# Revit family: 712-1520-001-DN80-250
name_source: partatom
category: Pipe Accessories
units: mm (PartAtom-declared; Revit-internal decimal feet)

## family parameters
Always vertical = Yes
Cut with Voids When Loaded = No
Part Type = Valve - Breaks Into
Round Connector Dimension = Use Diameter
Shared = No
Work Plane-Based = No

## types (8) — shared parameters
Body_wallthickness = 10 mm  [stored 0.0328084 ft]
DN080_PN10/16 = 712-0080-15-201
DN100_PN10/16 = 712-0100-15-201
DN125_PN10/16 = 712-0125-15-201
DN150_PN10/16 = 712-0150-15-201
DN200_PN10 = 712-0200-15-200
DN200_PN16 = 712-0200-15-201
DN250_PN10 = 712-0250-15-200
Description_ = AVK CROSS Loose flange
RF_Thick = 3 mm  [stored 0.00984252 ft]
Search_Table = 712-1520-001-DN80-250
URL product pages = https://www.avkvalves.com

## per-type parameters (varying)
| type | Ch | DN250_PN16 | FOD | Flange_thickness | H | ID(Radius) | L | Nominal Diameter (DN) | Rf_Dia | Rib |
| DN080_PN10/16 | 53 mm  [stored 0.173885 ft] | 712-0250-15-201 | 100 mm  [stored 0.328084 ft] | 19 mm  [stored 0.062336 ft] | 165 mm  [stored 0.541339 ft] | 40 mm  [stored 0.131234 ft] | 330 mm  [stored 1.08268 ft] | 80 mm  [stored 0.262467 ft] | 66 mm  [stored 0.216535 ft] | 10 mm  [stored 0.0328084 ft] |
| DN100_PN10/16 | 64 mm  [stored 0.209974 ft] | 712-0250-15-201 | 110 mm  [stored 0.360892 ft] | 19 mm  [stored 0.062336 ft] | 180 mm  [stored 0.590551 ft] | 50 mm  [stored 0.164042 ft] | 360 mm  [stored 1.1811 ft] | 100 mm  [stored 0.328084 ft] | 78 mm  [stored 0.255906 ft] | 10 mm  [stored 0.0328084 ft] |
| DN150_PN10/16 | 90 mm  [stored 0.295276 ft] | 712-0250-15-201 | 143 mm | 20 mm  [stored 0.0656168 ft] | 220 mm  [stored 0.721785 ft] | 75 mm | 440 mm | 150 mm  [stored 0.492126 ft] | 106 mm | 20 mm  [stored 0.0656168 ft] |
| DN200_PN10 | 117 mm | 712-0250-15-201 | 170 mm  [stored 0.557743 ft] | 20 mm  [stored 0.0656168 ft] | 260 mm  [stored 0.853018 ft] | 100 mm  [stored 0.328084 ft] | 520 mm | 200 mm  [stored 0.656168 ft] | 133 mm  [stored 0.436352 ft] | 25 mm  [stored 0.082021 ft] |
| DN200_PN16 | 117 mm | 712-0250-15-201
712-0250-15-201 | 170 mm  [stored 0.557743 ft] | 20 mm  [stored 0.0656168 ft] | 260 mm  [stored 0.853018 ft] | 100 mm  [stored 0.328084 ft] | 520 mm | 200 mm  [stored 0.656168 ft] | 133 mm  [stored 0.436352 ft] | 25 mm  [stored 0.082021 ft] |
| DN250_PN10 | 142 mm | 712-0250-15-201 | 200 mm  [stored 0.656168 ft] | 22 mm  [stored 0.0721785 ft] | 350 mm  [stored 1.14829 ft] | 125 mm  [stored 0.410105 ft] | 700 mm | 250 mm  [stored 0.82021 ft] | 160 mm  [stored 0.524934 ft] | 30 mm  [stored 0.0984252 ft] |
| DN250_PN16 | 142 mm | 712-0250-15-201 | 200 mm  [stored 0.656168 ft] | 22 mm  [stored 0.0721785 ft] | 350 mm  [stored 1.14829 ft] | 125 mm  [stored 0.410105 ft] | 700 mm | 250 mm  [stored 0.82021 ft] | 160 mm  [stored 0.524934 ft] | 30 mm  [stored 0.0984252 ft] |
| DN125_PN10/16 | 77 mm | 712-0250-15-201 | 125 mm  [stored 0.410105 ft] | 19 mm  [stored 0.062336 ft] | 200 mm  [stored 0.656168 ft] | 63 mm  [stored 0.206693 ft] | 400 mm | 125 mm  [stored 0.410105 ft] | 92 mm  [stored 0.301837 ft] | 15 mm  [stored 0.0492126 ft] |

note: [stored X ft] marks values corroborated as IEEE doubles in the binary element streams (Revit-internal decimal feet)

## geometry (parser evidence)
native form markers: Sweep x12
no freeform markers — native parametric forms only
